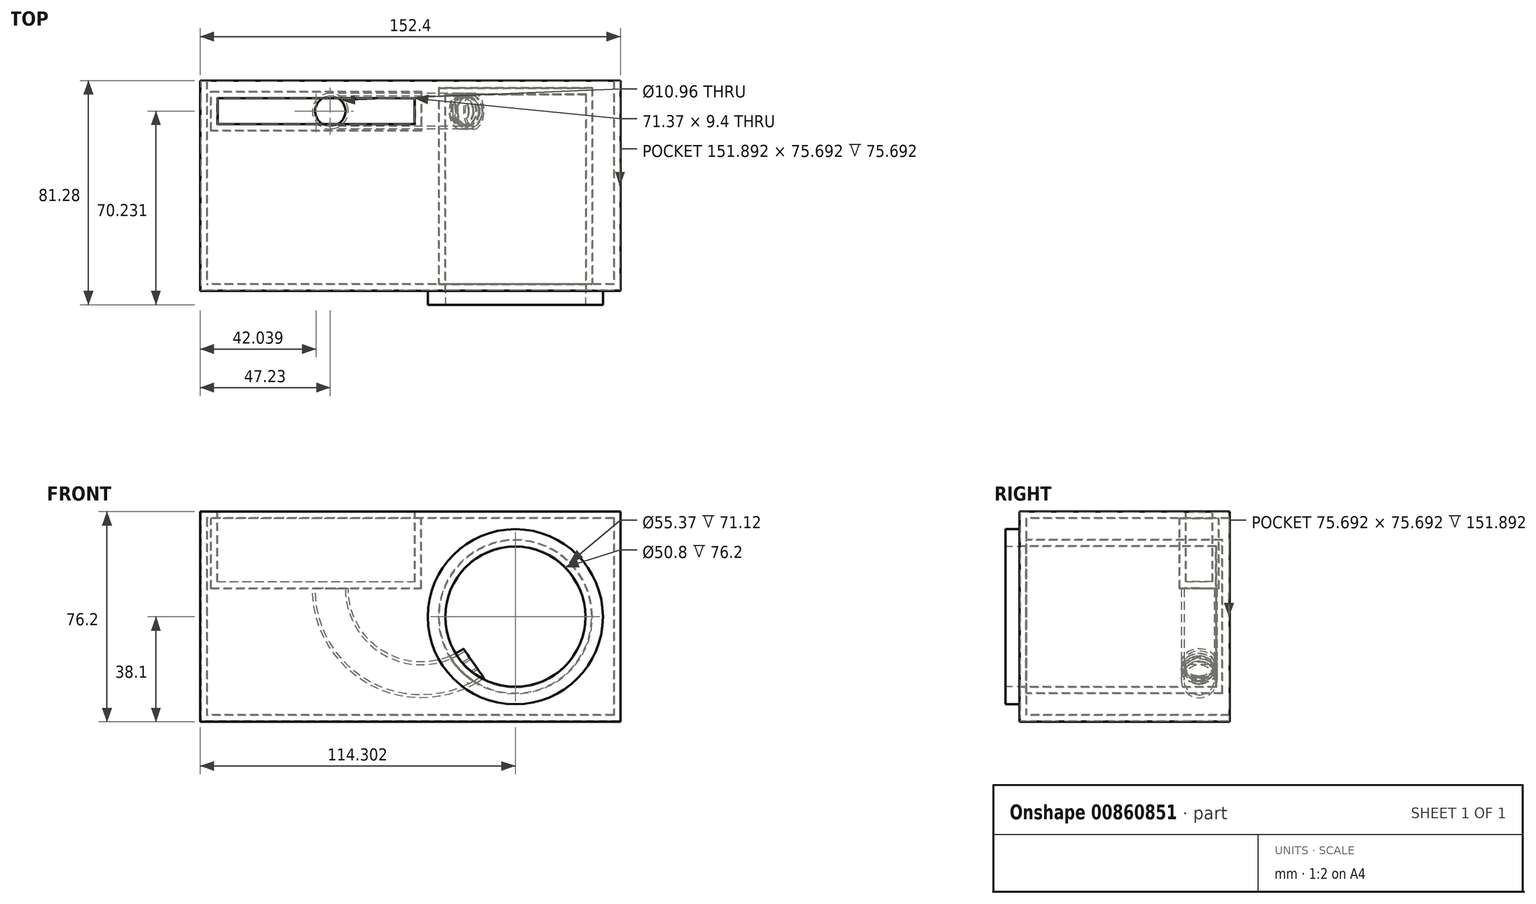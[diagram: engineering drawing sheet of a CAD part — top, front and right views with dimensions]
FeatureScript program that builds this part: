
annotation { "Feature Type Name" : "Feature", "Feature Type Description" : "" }
export const myFeature = defineFeature(function(context is Context, id is Id, definition is map)
    precondition{}
    {
        {
            var Q0;
            Q0=qCreatedBy(makeId("Top.planeOp"),FACE);
            var sketch = newSketch(context, id + "F0", { "sketchPlane" : qUnion([Q0])});
            skLineSegment(sketch, "E0.bottom", {"start": v(72.41, 0) * mm, "end": v(-79.99, 0) * mm});
            skLineSegment(sketch, "E0.top", {"start": v(72.41, -76.2) * mm, "end": v(-79.99, -76.2) * mm});
            skLineSegment(sketch, "E0.left", {"start": v(72.41, 0) * mm, "end": v(72.41, -76.2) * mm});
            skLineSegment(sketch, "E0.right", {"start": v(-79.99, 0) * mm, "end": v(-79.99, -76.2) * mm});
            skSolve(sketch);
        }
        {
            var Q0;
            Q0=makeQuery(id+"F0.imprint","IMPRINT",FACE,{"disambiguationData":[TD([[makeQuery(id+"F0.imprint","IMPRINT",EDGE,{"derivedFrom":sQuery(id+"F0.wireOp",EDGE,"E0.bottom")}),1.0]])]});
            extrude(context, id + "F1", {"entities" : qUnion([Q0]), "depth" : 76.2 * mm, "offsetDistance" : 25.4 * mm});
        }
        {
            var Q0;
            Q0=makeQuery(id+"F1.opExtrude","SWEPT_FACE",FACE,{"disambiguationData":[OSD([sQuery(id+"F0.wireOp",EDGE,"E0.top")])]});
            var sketch = newSketch(context, id + "F2", { "sketchPlane" : qUnion([Q0])});
            skLineSegment(sketch, "E1", {"start": v(-3.79, 0) * mm, "end": v(72.41, 0) * mm});
            skLineSegment(sketch, "E2", {"start": v(72.41, 0) * mm, "end": v(72.41, 76.2) * mm});
            skCircle(sketch, "E3", {"center": v(34.31, 38.1) * mm, "radius": 25.4 * mm});
            skPoint(sketch, "E3.centerSnap0", {"position": v(72.41, 38.1) * mm});
            skPoint(sketch, "E3.centerSnap1", {"position": v(34.31, 0) * mm});
            skCircle(sketch, "E4", {"center": v(34.31, 38.1) * mm, "radius": 31.75 * mm});
            skSolve(sketch);
        }
        {
            var Q0;
            Q0=makeQuery(id+"F2.imprint","IMPRINT",FACE,{"disambiguationData":[TD([[makeQuery(id+"F2.imprint","IMPRINT",EDGE,{"derivedFrom":sQuery(id+"F2.wireOp",EDGE,"E3")}),1.0]])]});
            extrude(context, id + "F3", {"entities" : qUnion([Q0]), "operationType" : NewBodyOperationType.REMOVE, "oppositeDirection" : true, "depth" : 71.12 * mm, "offsetDistance" : 25.4 * mm});
        }
        {
            var Q0;
            Q0=makeQuery(id+"F1.opExtrude","CAP_FACE",FACE,{"disambiguationData":[OSD([sQuery(id+"F0.wireOp",EDGE,"E0.bottom"),sQuery(id+"F0.wireOp",EDGE,"E0.top"),sQuery(id+"F0.wireOp",EDGE,"E0.left"),sQuery(id+"F0.wireOp",EDGE,"E0.right")])],"isStart":false});
            var sketch = newSketch(context, id + "F4", { "sketchPlane" : qUnion([Q0])});
            skLineSegment(sketch, "E5", {"start": v(-79.99, 0) * mm, "end": v(-73.64, 0) * mm});
            skLineSegment(sketch, "E6", {"start": v(-73.64, 0) * mm, "end": v(-73.64, -6.35) * mm});
            skLineSegment(sketch, "E7", {"start": v(-73.64, -6.35) * mm, "end": v(-2.26, -6.35) * mm});
            skLineSegment(sketch, "E8", {"start": v(-2.26, -6.35) * mm, "end": v(-2.26, -15.75) * mm});
            skLineSegment(sketch, "E9", {"start": v(-2.26, -15.75) * mm, "end": v(-73.64, -15.75) * mm});
            skLineSegment(sketch, "E10", {"start": v(-73.64, -15.75) * mm, "end": v(-73.64, -6.35) * mm});
            skSolve(sketch);
        }
        {
            var Q0;
            Q0=makeQuery(id+"F4.imprint","IMPRINT",FACE,{"disambiguationData":[TD([[makeQuery(id+"F4.imprint","IMPRINT",EDGE,{"derivedFrom":sQuery(id+"F4.wireOp",EDGE,"E7")}),-1.0]])]});
            extrude(context, id + "F5", {"entities" : qUnion([Q0]), "operationType" : NewBodyOperationType.REMOVE, "oppositeDirection" : true, "depth" : 25.4 * mm, "offsetDistance" : 25.4 * mm});
        }
        {
            var Q0;
            Q0=makeQuery(id+"F1.opExtrude","SWEPT_FACE",FACE,{"disambiguationData":[OSD([sQuery(id+"F0.wireOp",EDGE,"E0.bottom")])]});
            shell(context, id + "F6", {"entities" : qUnion([Q0]), "thickness" : 2.54 * mm});
        }
        {
            var Q0;
            Q0=makeQuery(id+"F5.boolean.opBoolean","COPY",FACE,{"derivedFrom":makeQuery(id+"F5.opExtrude","CAP_FACE",FACE,{"disambiguationData":[OSD([sQuery(id+"F4.wireOp",EDGE,"E7"),sQuery(id+"F4.wireOp",EDGE,"E8"),sQuery(id+"F4.wireOp",EDGE,"E9"),sQuery(id+"F4.wireOp",EDGE,"E10")])],"isStart":false})});
            shell(context, id + "F7", {"entities" : qUnion([Q0]), "thickness" : 0.25 * mm});
        }
        {
            var Q0;
            Q0=makeQuery(id+"F2.imprint","IMPRINT",FACE,{"disambiguationData":[TD([[makeQuery(id+"F2.imprint","IMPRINT",EDGE,{"derivedFrom":sQuery(id+"F2.wireOp",EDGE,"E3")}),-1.0]])]});
            extrude(context, id + "F8", {"entities" : qUnion([Q0]), "operationType" : NewBodyOperationType.ADD, "depth" : 5.08 * mm, "offsetDistance" : 25.4 * mm});
        }
        {
            var Q0;
            Q0=makeQuery(id+"F6.opShell","OFFSET_FACE",FACE,{"disambiguationData":[OSD([sQuery(id+"F4.wireOp",EDGE,"E7"),sQuery(id+"F4.wireOp",EDGE,"E8"),sQuery(id+"F4.wireOp",EDGE,"E9"),sQuery(id+"F4.wireOp",EDGE,"E10")])]});
            var sketch = newSketch(context, id + "F9", { "sketchPlane" : qUnion([Q0])});
            skFitSpline(sketch, "E11", {"points": [v(-19.78, 37.54) * mm, v(-20.67, 36.73) * mm], "startDerivative": vector(-0.88, -0.81) * mm, "endDerivative": vector(-0.88, -0.81) * mm});
            skCircle(sketch, "E12", {"center": v(-32.76, 11.05) * mm, "radius": 6.5 * mm});
            skPoint(sketch, "E12.centerSnap0", {"position": v(0.28, 11.05) * mm});
            skCircle(sketch, "E13.0", {"center": v(-32.76, 11.05) * mm, "radius": 5.48 * mm});
            skSolve(sketch);
        }
        {
            var Q0;
            Q0=makeQuery(id+"F9.imprint","IMPRINT",FACE,{"disambiguationData":[TD([[makeQuery(id+"F9.imprint","IMPRINT",EDGE,{"derivedFrom":sQuery(id+"F9.wireOp",EDGE,"E12")}),1.0]])]});
            var Q1;
            {var subQ0=sQuery(id+"F4.wireOp",EDGE,"E8");Q1=makeQuery(id+"F6.opShell","OFFSET_EDGE",EDGE,{"disambiguationData":[OSD([subQ0]),TDD([makeQuery(id+"F5.boolean.opBoolean","COPY",EDGE,{"derivedFrom":makeQuery(id+"F5.opExtrude","CAP_EDGE",EDGE,{"disambiguationData":[OSD([subQ0])],"isStart":false})})])]});}
            revolve(context, id + "F10", {"operationType" : NewBodyOperationType.ADD, "surfaceOperationType" : NewSurfaceOperationType.NEW, "entities" : qUnion([Q0]), "axis" : qUnion([Q1]), "revolveType" : RevolveType.ONE_DIRECTION, "angle" : 125 * degree});
        }
        {
            var Q0;
            Q0=makeQuery(id+"F9.imprint","IMPRINT",FACE,{"disambiguationData":[TD([[makeQuery(id+"F9.imprint","IMPRINT",EDGE,{"derivedFrom":sQuery(id+"F9.wireOp",EDGE,"E13.0")}),1.0]])]});
            extrude(context, id + "F11", {"entities" : qUnion([Q0]), "operationType" : NewBodyOperationType.REMOVE, "oppositeDirection" : true, "depth" : 1.27 * mm, "offsetDistance" : 25.4 * mm});
        }
        {
            var Q0;
            {var subQ0=sQuery(id+"F9.wireOp",EDGE,"E12");var subQ1=sQuery(id+"F9.wireOp",EDGE,"E13.0");Q0=makeQuery(id+"F10.boolean.opBoolean","SPLIT",FACE,{"disambiguationData":[TD([makeQuery(id+"F3.boolean.opBoolean","COPY",FACE,{"derivedFrom":makeQuery(id+"F3.opExtrude","CAP_FACE",FACE,{"disambiguationData":[OSD([sQuery(id+"F2.wireOp",EDGE,"E3")])],"isStart":false})})])],"derivedFrom":makeQuery(id+"F10.opRevolve","CAP_FACE",FACE,{"disambiguationData":[OSD([subQ0,subQ1])],"isStart":false})});}
            var sketch = newSketch(context, id + "F12", { "sketchPlane" : qUnion([Q0])});
            skCircle(sketch, "E14", {"center": v(-11.05, 6.34) * mm, "radius": 5.08 * mm});
            skSolve(sketch);
        }
        {
            var Q0;
            Q0=makeQuery(id+"F12.imprint","IMPRINT",FACE,{"disambiguationData":[TD([[makeQuery(id+"F12.imprint","IMPRINT",EDGE,{"derivedFrom":sQuery(id+"F12.wireOp",EDGE,"E14")}),1.0]])]});
            extrude(context, id + "F13", {"entities" : qUnion([Q0]), "operationType" : NewBodyOperationType.REMOVE, "oppositeDirection" : true, "depth" : 5.84 * mm, "offsetDistance" : 25.4 * mm});
        }
    });
